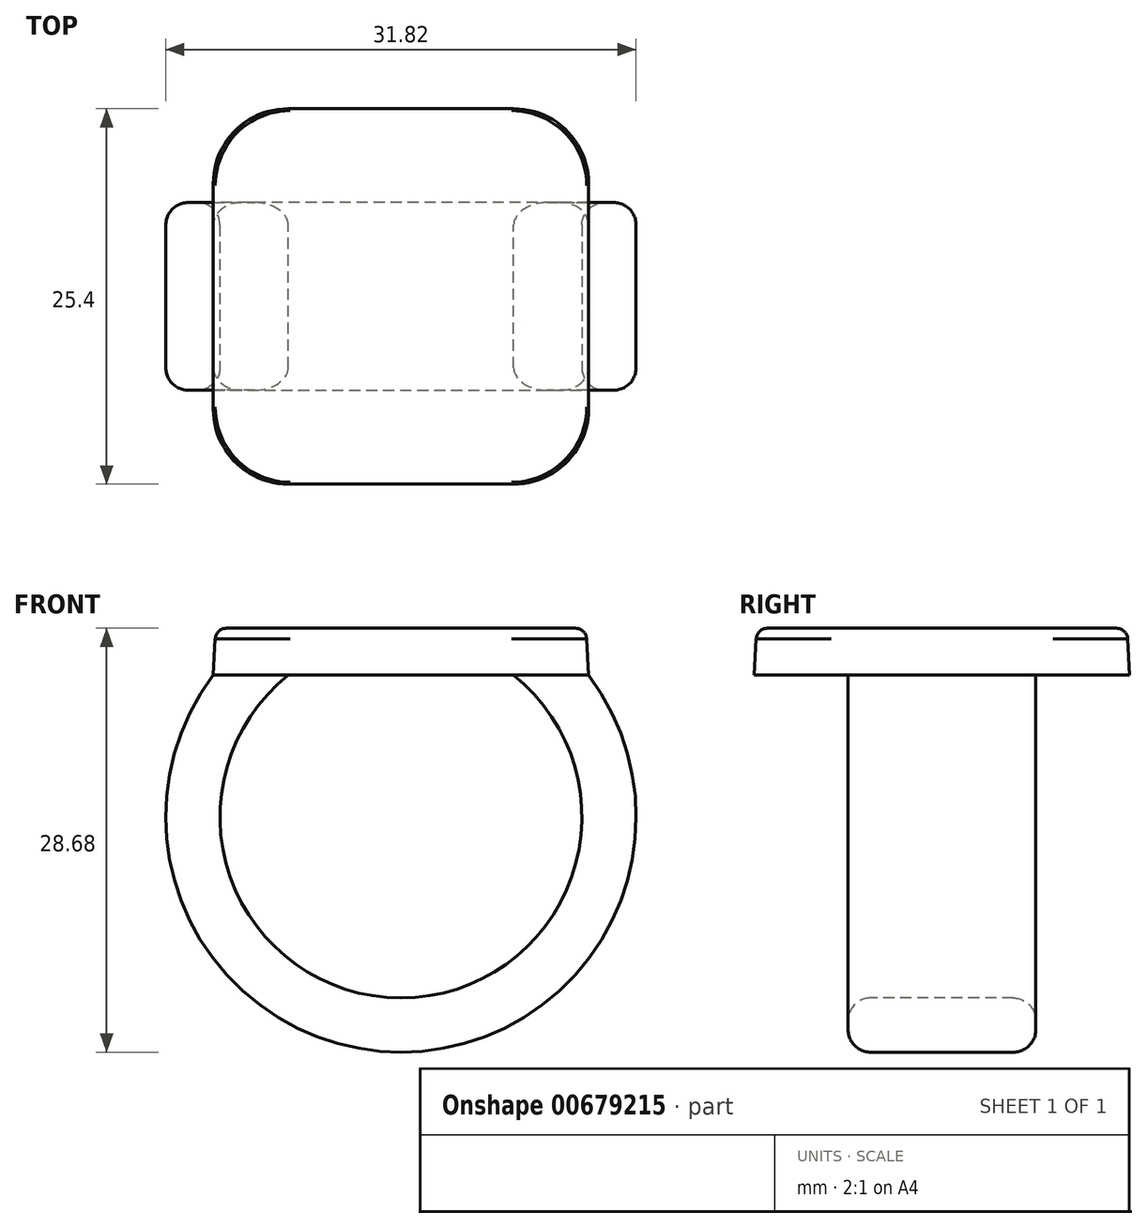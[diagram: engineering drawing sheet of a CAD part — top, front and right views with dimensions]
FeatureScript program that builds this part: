
annotation { "Feature Type Name" : "Feature", "Feature Type Description" : "" }
export const myFeature = defineFeature(function(context is Context, id is Id, definition is map)
    precondition{}
    {
        {
            var Q0;
            Q0=qCreatedBy(makeId("Top.planeOp"),FACE);
            var sketch = newSketch(context, id + "F0", { "sketchPlane" : qUnion([Q0])});
            skLineSegment(sketch, "E0.bottom", {"start": v(12.7, 12.7) * mm, "end": v(-12.7, 12.7) * mm});
            skLineSegment(sketch, "E0.top", {"start": v(12.7, -12.7) * mm, "end": v(-12.7, -12.7) * mm});
            skLineSegment(sketch, "E0.left", {"start": v(12.7, 12.7) * mm, "end": v(12.7, -12.7) * mm});
            skLineSegment(sketch, "E0.right", {"start": v(-12.7, 12.7) * mm, "end": v(-12.7, -12.7) * mm});
            skPoint(sketch, "E0.middle", {"position": v(0, 0) * mm});
            skSolve(sketch);
        }
        {
            var Q0;
            Q0 = qSketchRegion(id + "F0", true);
            extrude(context, id + "F1", {"entities" : qUnion([Q0]), "depth" : 3.17 * mm, "offsetDistance" : 25.4 * mm, "hasDraft" : true, "draftAngle" : 3 * degree, "draftPullDirection" : true});
        }
        {
            var Q0;
            Q0=qCreatedBy(makeId("Front.planeOp"),FACE);
            var sketch = newSketch(context, id + "F2", { "sketchPlane" : qUnion([Q0])});
            skArc(sketch, "E1", {"start": v(-10.16, 0) * mm, "mid": v(0, -23.56) * mm, "end": v(10.16, 0) * mm});
            skSolve(sketch);
        }
        {
            var Q0;
            Q0=makeQuery(id+"F1.opExtrude","CAP_FACE",FACE,{"disambiguationData":[OSD([sQuery(id+"F0.wireOp",EDGE,"E0.bottom"),sQuery(id+"F0.wireOp",EDGE,"E0.top"),sQuery(id+"F0.wireOp",EDGE,"E0.left"),sQuery(id+"F0.wireOp",EDGE,"E0.right")])],"isStart":true});
            var sketch = newSketch(context, id + "F3", { "sketchPlane" : qUnion([Q0])});
            skLineSegment(sketch, "E2.bottom", {"start": v(-7.62, 6.35) * mm, "end": v(-12.7, 6.35) * mm});
            skLineSegment(sketch, "E2.top", {"start": v(-7.62, -6.35) * mm, "end": v(-12.7, -6.35) * mm});
            skLineSegment(sketch, "E2.left", {"start": v(-7.62, 6.35) * mm, "end": v(-7.62, -6.35) * mm});
            skLineSegment(sketch, "E2.right", {"start": v(-12.7, 6.35) * mm, "end": v(-12.7, -6.35) * mm});
            skPoint(sketch, "E2.middle", {"position": v(-10.16, 0) * mm});
            skSolve(sketch);
        }
        {
            var Q0;
            Q0 = qSketchRegion(id + "F3", true);
            var Q1;
            Q1 = qConstructionFilter(qBodyType(qCreatedBy(id + "F2" ,EDGE), BodyType.WIRE), ConstructionObject.NO);
            sweep(context, id + "F4", {"operationType" : NewBodyOperationType.ADD, "profiles" : qUnion([Q0]), "path" : qUnion([Q1])});
        }
        {
            var Q0;
            Q0=qCreatedBy(makeId("Front.planeOp"),FACE);
            var sketch = newSketch(context, id + "F5", { "sketchPlane" : qUnion([Q0])});
            skLineSegment(sketch, "E3.0", {"start": v(10.16, 0) * mm, "end": v(7.62, 0) * mm});
            skLineSegment(sketch, "E3.1", {"start": v(10.01, -2.54) * mm, "end": v(10.16, 0) * mm});
            skArc(sketch, "E3.2", {"start": v(10.01, -2.54) * mm, "mid": v(8.9, -1.18) * mm, "end": v(7.62, 0) * mm});
            skSolve(sketch);
        }
        {
            var Q0;
            Q0 = qSketchRegion(id + "F5", true);
            var Q1;
            Q1=makeQuery(id+"F4.opSweep","SWEPT_FACE",FACE,{"disambiguationData":[OSD([sQuery(id+"F2.wireOp",EDGE,"E1"),sQuery(id+"F3.wireOp",EDGE,"E2.bottom")])]});
            var Q2;
            Q2=makeQuery(id+"F4.opSweep","SWEPT_FACE",FACE,{"disambiguationData":[OSD([sQuery(id+"F2.wireOp",EDGE,"E1"),sQuery(id+"F3.wireOp",EDGE,"E2.top")])]});
            extrude(context, id + "F6", {"entities" : qUnion([Q0]), "operationType" : NewBodyOperationType.ADD, "endBound" : BoundingType.UP_TO_SURFACE, "depth" : 25.4 * mm, "endBoundEntityFace" : qUnion([Q1]), "offsetDistance" : 25.4 * mm, "hasSecondDirection" : true, "secondDirectionBound" : SecondDirectionBoundingType.UP_TO_SURFACE, "secondDirectionOppositeDirection" : true, "secondDirectionDepth" : 25.4 * mm, "secondDirectionBoundEntityFace" : qUnion([Q2])});
        }
        {
            var Q0;
            Q0=makeQuery(id+"F1.opExtrude","SWEPT_EDGE",EDGE,{"disambiguationData":[OSD([sQuery(id+"F0.wireOp",EDGE,"E0.top"),sQuery(id+"F0.wireOp",EDGE,"E0.left")])]});
            var Q1;
            Q1=makeQuery(id+"F1.opExtrude","SWEPT_EDGE",EDGE,{"disambiguationData":[OSD([sQuery(id+"F0.wireOp",EDGE,"E0.bottom"),sQuery(id+"F0.wireOp",EDGE,"E0.left")])]});
            var Q2;
            Q2=makeQuery(id+"F1.opExtrude","SWEPT_EDGE",EDGE,{"disambiguationData":[OSD([sQuery(id+"F0.wireOp",EDGE,"E0.bottom"),sQuery(id+"F0.wireOp",EDGE,"E0.right")])]});
            var Q3;
            Q3=makeQuery(id+"F1.opExtrude","SWEPT_EDGE",EDGE,{"disambiguationData":[OSD([sQuery(id+"F0.wireOp",EDGE,"E0.top"),sQuery(id+"F0.wireOp",EDGE,"E0.right")])]});
            fillet(context, id + "F7", {"entities" : qUnion([Q0, Q1, Q2, Q3]), "radius" : 5.08 * mm, "tangentPropagation" : true, "allowEdgeOverflow" : false});
        }
        {
            var Q0;
            {var subQ0=sQuery(id+"F3.wireOp",EDGE,"E2.bottom");var subQ1=sQuery(id+"F2.wireOp",EDGE,"E1");Q0=makeQuery(id+"F6.boolean.opBoolean","MERGE",EDGE,{"derivedFrom":[makeQuery(id+"F4.opSweep","SWEPT_EDGE",EDGE,{"disambiguationData":[OSD([subQ1,subQ0,sQuery(id+"F3.wireOp",EDGE,"E2.left")])]}),makeQuery(id+"F6.opExtrude","TWEAK_EDGE",EDGE,{"derivedFrom":[makeQuery(id+"F4.opSweep","SWEPT_FACE",FACE,{"disambiguationData":[OSD([subQ1,subQ0])]}),makeQuery(id+"F5.imprint","IMPRINT",EDGE,{"derivedFrom":sQuery(id+"F5.wireOp",EDGE,"E3.2")})]})]});}
            var Q1;
            Q1=makeQuery(id+"F4.opSweep","SWEPT_EDGE",EDGE,{"disambiguationData":[OSD([sQuery(id+"F0.wireOp",EDGE,"E0.right"),sQuery(id+"F2.wireOp",EDGE,"E1"),sQuery(id+"F3.wireOp",EDGE,"E2.bottom"),sQuery(id+"F3.wireOp",EDGE,"E2.right")])]});
            var Q2;
            Q2=makeQuery(id+"F4.opSweep","SWEPT_EDGE",EDGE,{"disambiguationData":[OSD([sQuery(id+"F0.wireOp",EDGE,"E0.right"),sQuery(id+"F2.wireOp",EDGE,"E1"),sQuery(id+"F3.wireOp",EDGE,"E2.top"),sQuery(id+"F3.wireOp",EDGE,"E2.right")])]});
            var Q3;
            {var subQ0=sQuery(id+"F3.wireOp",EDGE,"E2.top");var subQ1=sQuery(id+"F2.wireOp",EDGE,"E1");Q3=makeQuery(id+"F6.boolean.opBoolean","MERGE",EDGE,{"derivedFrom":[makeQuery(id+"F4.opSweep","SWEPT_EDGE",EDGE,{"disambiguationData":[OSD([subQ1,subQ0,sQuery(id+"F3.wireOp",EDGE,"E2.left")])]}),makeQuery(id+"F6.opExtrude","TWEAK_EDGE",EDGE,{"derivedFrom":[makeQuery(id+"F4.opSweep","SWEPT_FACE",FACE,{"disambiguationData":[OSD([subQ1,subQ0])]}),makeQuery(id+"F5.imprint","IMPRINT",EDGE,{"derivedFrom":sQuery(id+"F5.wireOp",EDGE,"E3.2")})]})]});}
            fillet(context, id + "F8", {"entities" : qUnion([Q0, Q1, Q2, Q3]), "radius" : 1.52 * mm, "tangentPropagation" : true, "allowEdgeOverflow" : false});
        }
        {
            var Q0;
            Q0=makeQuery(id+"F1.opExtrude","CAP_FACE",FACE,{"disambiguationData":[OSD([sQuery(id+"F0.wireOp",EDGE,"E0.bottom"),sQuery(id+"F0.wireOp",EDGE,"E0.top"),sQuery(id+"F0.wireOp",EDGE,"E0.left"),sQuery(id+"F0.wireOp",EDGE,"E0.right")])],"isStart":false});
            fillet(context, id + "F9", {"entities" : qUnion([Q0]), "radius" : 0.76 * mm, "tangentPropagation" : true, "allowEdgeOverflow" : false});
        }
    });
